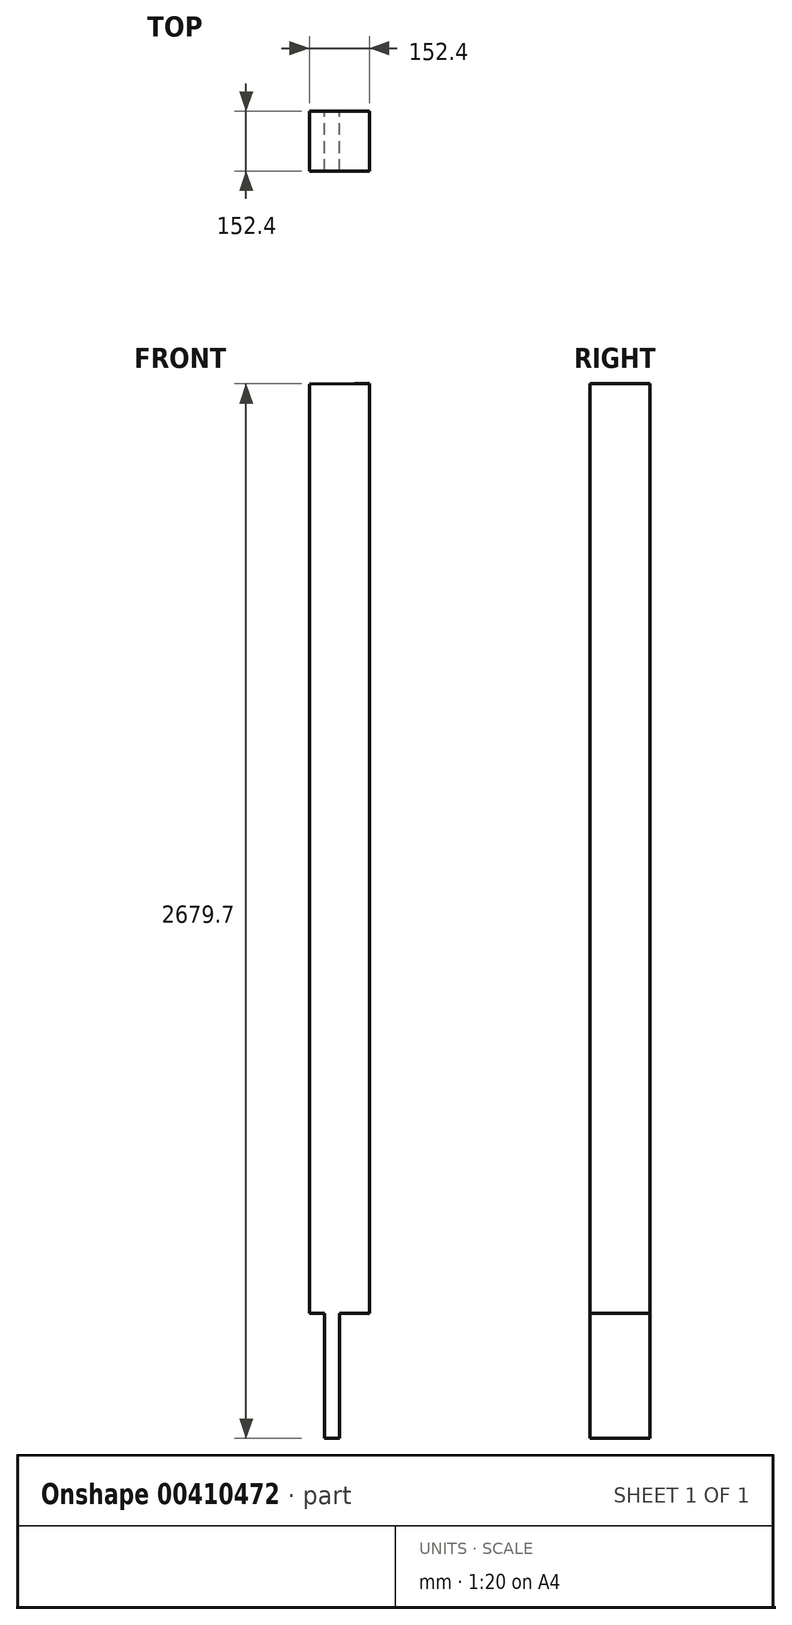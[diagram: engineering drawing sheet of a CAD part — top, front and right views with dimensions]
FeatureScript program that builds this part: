
annotation { "Feature Type Name" : "Feature", "Feature Type Description" : "" }
export const myFeature = defineFeature(function(context is Context, id is Id, definition is map)
    precondition{}
    {
        {
            var Q0;
            Q0=qCreatedBy(makeId("Front.planeOp"),FACE);
            var sketch = newSketch(context, id + "F0", { "sketchPlane" : qUnion([Q0])});
            skLineSegment(sketch, "E0.bottom", {"start": v(-76.2, 1225.1) * mm, "end": v(76.2, 1225.1) * mm});
            skLineSegment(sketch, "E0.top", {"start": v(-76.2, -1225.1) * mm, "end": v(76.2, -1225.1) * mm});
            skLineSegment(sketch, "E0.left", {"start": v(-76.2, 1225.1) * mm, "end": v(-76.2, -1225.1) * mm});
            skLineSegment(sketch, "E0.right", {"start": v(76.2, 1225.1) * mm, "end": v(76.2, -1225.1) * mm});
            skPoint(sketch, "E0.middle", {"position": v(0, 0) * mm});
            skLineSegment(sketch, "E1", {"start": v(-76.2, 1136.2) * mm, "end": v(38.1, 1137.1) * mm});
            skPoint(sketch, "E2.middle", {"position": v(0, 1092.2) * mm});
            skLineSegment(sketch, "E3.bottom", {"start": v(-19.05, 1136.65) * mm, "end": v(19.05, 1136.65) * mm});
            skLineSegment(sketch, "E3.top", {"start": v(-19.05, 1225.1) * mm, "end": v(19.05, 1225.1) * mm});
            skLineSegment(sketch, "E3.left", {"start": v(-19.05, 1136.65) * mm, "end": v(-19.05, 1225.1) * mm});
            skLineSegment(sketch, "E3.right", {"start": v(19.05, 1136.65) * mm, "end": v(19.05, 1225.1) * mm});
            skLineSegment(sketch, "E4", {"start": v(38.1, 1137.1) * mm, "end": v(76.2, 1137.1) * mm});
            skSolve(sketch);
        }
        {
            var Q0;
            {var subQ1=sQuery(id+"F0.wireOp",EDGE,"E0.top");Q0=makeQuery(id+"F0.imprint","IMPRINT",FACE,{"disambiguationData":[TD([[makeQuery(id+"F0.imprint","IMPRINT",EDGE,{"derivedFrom":subQ1}),1.0]])]});}
            var Q1;
            Q1=makeQuery(id+"F0.imprint","IMPRINT",FACE,{"disambiguationData":[TD([[makeQuery(id+"F0.imprint","IMPRINT",EDGE,{"derivedFrom":sQuery(id+"F0.wireOp",EDGE,"OlOpib3l-DV6w-VdAR-WjI2-fuE5ldOcum9m.bottom")}),1.0]])]});
            var Q2;
            Q2=makeQuery(id+"F0.imprint","IMPRINT",FACE,{"disambiguationData":[TD([[makeQuery(id+"F0.imprint","IMPRINT",EDGE,{"derivedFrom":sQuery(id+"F0.wireOp",EDGE,"E2.bottom")}),1.0]])]});
            var Q3;
            Q3=makeQuery(id+"F0.imprint","IMPRINT",FACE,{"disambiguationData":[TD([[makeQuery(id+"F0.imprint","IMPRINT",EDGE,{"derivedFrom":sQuery(id+"F0.wireOp",EDGE,"E3.bottom")}),1.0]])]});
            var Q4;
            {var subQ4=sQuery(id+"F0.wireOp",EDGE,"E3.top");Q4=makeQuery(id+"F0.imprint","IMPRINT",FACE,{"disambiguationData":[TD([[makeQuery(id+"F0.imprint","IMPRINT",EDGE,{"derivedFrom":subQ4}),-1.0]])]});}
            extrude(context, id + "F1", {"entities" : qUnion([Q0, Q1, Q2, Q3, Q4]), "offsetDistance" : 25.4 * mm, "depth" : 152.4 * mm, "symmetric" : true});
        }
        {
            var Q0;
            Q0=makeQuery(id+"F1.opExtrude","SWEPT_FACE",FACE,{"disambiguationData":[OSD([sQuery(id+"F0.wireOp",EDGE,"E0.top")])]});
            var sketch = newSketch(context, id + "F2", { "sketchPlane" : qUnion([Q0])});
            skLineSegment(sketch, "E5.bottom", {"start": v(0, 76.2) * mm, "end": v(-38.1, 76.2) * mm});
            skLineSegment(sketch, "E5.top", {"start": v(0, -76.2) * mm, "end": v(-38.1, -76.2) * mm});
            skLineSegment(sketch, "E5.left", {"start": v(0, 76.2) * mm, "end": v(0, -76.2) * mm});
            skLineSegment(sketch, "E5.right", {"start": v(-38.1, 76.2) * mm, "end": v(-38.1, -76.2) * mm});
            skSolve(sketch);
        }
        {
            var Q0;
            Q0 = qSketchRegion(id + "F2", true);
            extrude(context, id + "F3", {"entities" : qUnion([Q0]), "operationType" : NewBodyOperationType.ADD, "depth" : 317.5 * mm, "offsetDistance" : 25.4 * mm});
        }
    });
